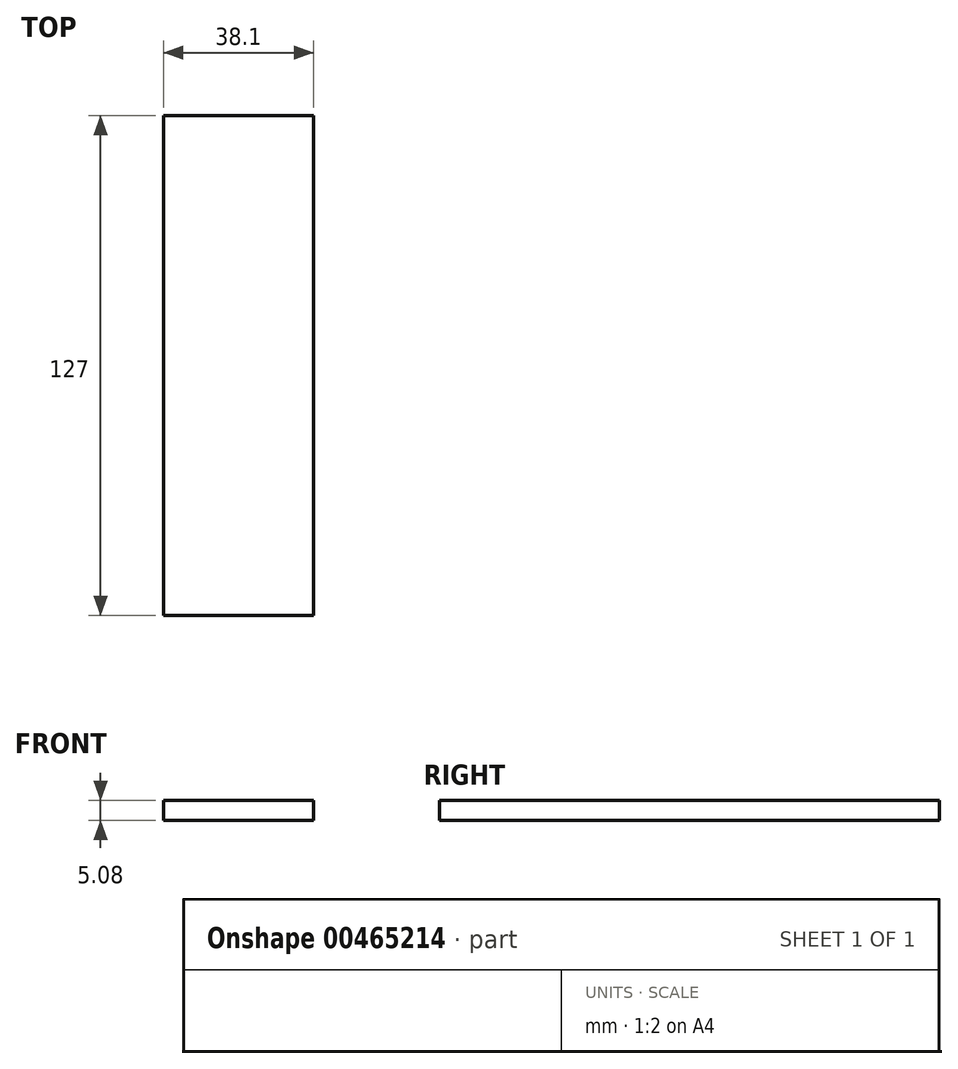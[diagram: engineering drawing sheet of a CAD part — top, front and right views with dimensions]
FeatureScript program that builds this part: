
annotation { "Feature Type Name" : "Feature", "Feature Type Description" : "" }
export const myFeature = defineFeature(function(context is Context, id is Id, definition is map)
    precondition{}
    {
        {
            var Q0;
            Q0=qCreatedBy(makeId("Front.planeOp"),FACE);
            var sketch = newSketch(context, id + "F0", { "sketchPlane" : qUnion([Q0])});
            skLineSegment(sketch, "E0.bottom", {"start": v(19.05, 2.54) * mm, "end": v(-19.05, 2.54) * mm});
            skLineSegment(sketch, "E0.top", {"start": v(19.05, -2.54) * mm, "end": v(-19.05, -2.54) * mm});
            skLineSegment(sketch, "E0.left", {"start": v(19.05, 2.54) * mm, "end": v(19.05, -2.54) * mm});
            skLineSegment(sketch, "E0.right", {"start": v(-19.05, 2.54) * mm, "end": v(-19.05, -2.54) * mm});
            skPoint(sketch, "E0.middle", {"position": v(0, 0) * mm});
            skSolve(sketch);
        }
        {
            var Q0;
            Q0 = qSketchRegion(id + "F0", true);
            extrude(context, id + "F1", {"entities" : qUnion([Q0]), "depth" : 127 * mm});
        }
    });
